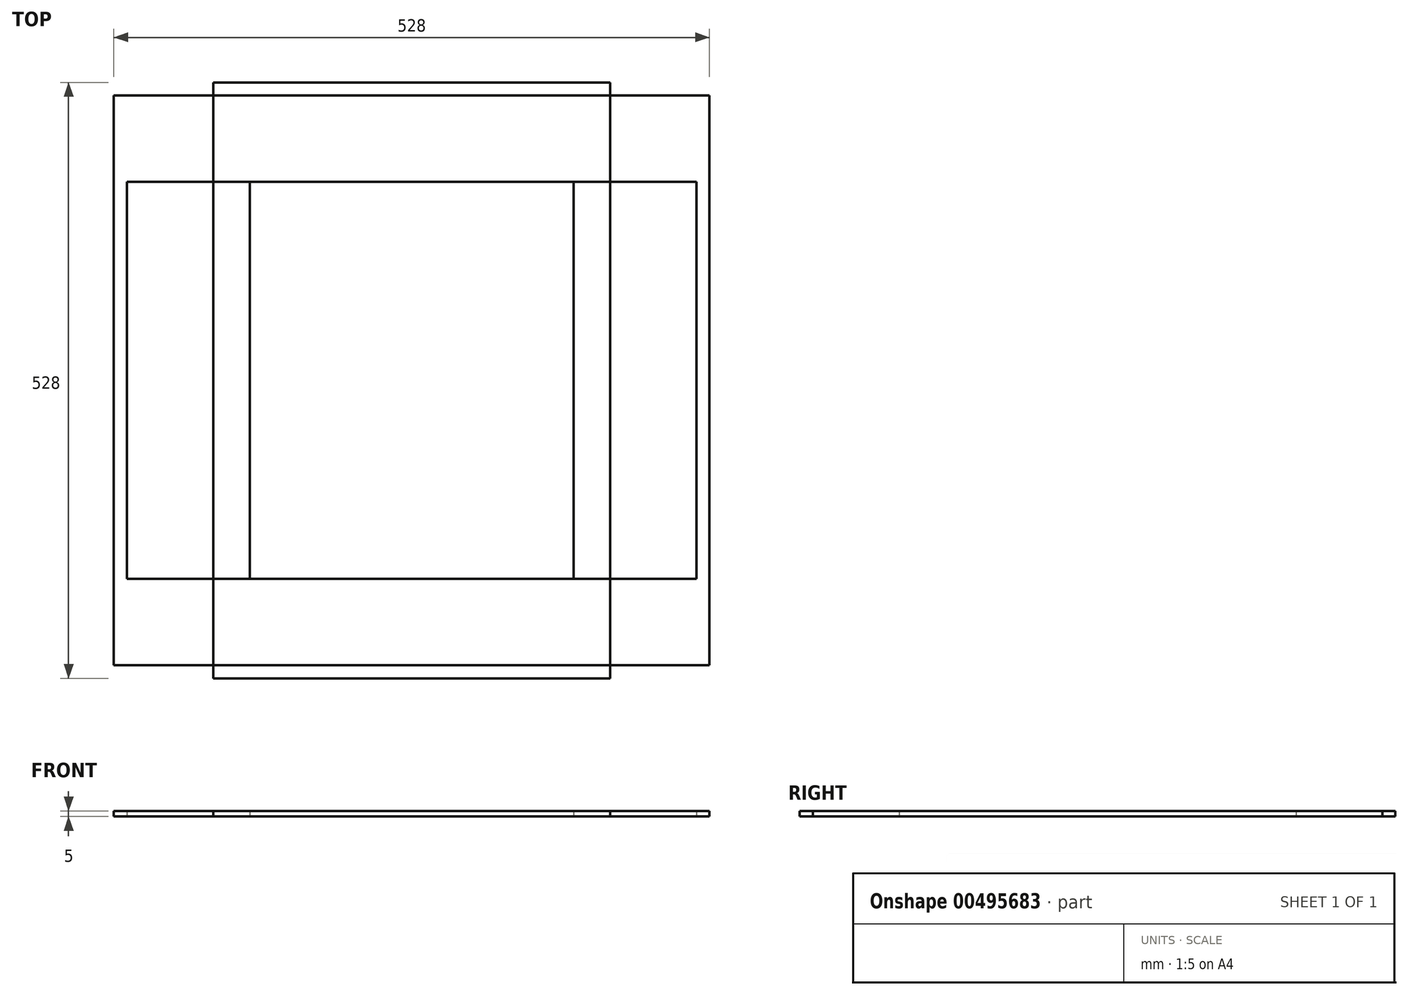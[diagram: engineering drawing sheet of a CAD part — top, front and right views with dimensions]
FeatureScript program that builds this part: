
annotation { "Feature Type Name" : "Feature", "Feature Type Description" : "" }
export const myFeature = defineFeature(function(context is Context, id is Id, definition is map)
    precondition{}
    {
        {
            var Q0;
            Q0=qCreatedBy(makeId("Top.planeOp"),FACE);
            var sketch = newSketch(context, id + "F0", { "sketchPlane" : qUnion([Q0])});
            skLineSegment(sketch, "E0.bottom", {"start": v(252.5, 176) * mm, "end": v(-252.5, 176) * mm});
            skLineSegment(sketch, "E0.top", {"start": v(252.5, -176) * mm, "end": v(-252.5, -176) * mm});
            skLineSegment(sketch, "E0.left", {"start": v(252.5, 176) * mm, "end": v(252.5, -176) * mm});
            skLineSegment(sketch, "E0.right", {"start": v(-252.5, 176) * mm, "end": v(-252.5, -176) * mm});
            skPoint(sketch, "E0.middle", {"position": v(0, 0) * mm});
            skSolve(sketch);
        }
        {
            var Q0;
            Q0 = qSketchRegion(id + "F0", true);
            extrude(context, id + "F1", {"entities" : qUnion([Q0]), "depth" : 5 * mm});
        }
        {
            var Q0;
            Q0=qCreatedBy(makeId("Top.planeOp"),FACE);
            var sketch = newSketch(context, id + "F2", { "sketchPlane" : qUnion([Q0])});
            skLineSegment(sketch, "E1.bottom", {"start": v(264, 252.5) * mm, "end": v(-264, 252.5) * mm});
            skLineSegment(sketch, "E1.top", {"start": v(264, -252.5) * mm, "end": v(-264, -252.5) * mm});
            skLineSegment(sketch, "E1.left", {"start": v(264, 252.5) * mm, "end": v(264, -252.5) * mm});
            skLineSegment(sketch, "E1.right", {"start": v(-264, 252.5) * mm, "end": v(-264, -252.5) * mm});
            skPoint(sketch, "E1.middle", {"position": v(0, 0) * mm});
            skSolve(sketch);
        }
        {
            var Q0;
            Q0=makeQuery(id+"F2.imprint","IMPRINT",FACE,{"disambiguationData":[TD([[makeQuery(id+"F2.imprint","IMPRINT",EDGE,{"derivedFrom":sQuery(id+"F2.wireOp",EDGE,"E1.bottom")}),1.0]])]});
            extrude(context, id + "F3", {"entities" : qUnion([Q0]), "depth" : 5 * mm});
        }
        {
            var Q0;
            Q0=qCreatedBy(makeId("Top.planeOp"),FACE);
            var sketch = newSketch(context, id + "F4", { "sketchPlane" : qUnion([Q0])});
            skLineSegment(sketch, "E2.bottom", {"start": v(176, 264) * mm, "end": v(-176, 264) * mm});
            skLineSegment(sketch, "E2.top", {"start": v(176, -264) * mm, "end": v(-176, -264) * mm});
            skLineSegment(sketch, "E2.left", {"start": v(176, 264) * mm, "end": v(176, -264) * mm});
            skLineSegment(sketch, "E2.right", {"start": v(-176, 264) * mm, "end": v(-176, -264) * mm});
            skPoint(sketch, "E2.middle", {"position": v(0, 0) * mm});
            skSolve(sketch);
        }
        {
            var Q0;
            Q0 = qSketchRegion(id + "F4", true);
            extrude(context, id + "F5", {"entities" : qUnion([Q0]), "depth" : 5 * mm});
        }
        {
            var Q0;
            Q0=qCreatedBy(makeId("Top.planeOp"),FACE);
            var sketch = newSketch(context, id + "F6", { "sketchPlane" : qUnion([Q0])});
            skLineSegment(sketch, "E3.bottom", {"start": v(143.5, 176) * mm, "end": v(-143.5, 176) * mm});
            skLineSegment(sketch, "E3.top", {"start": v(143.5, -176) * mm, "end": v(-143.5, -176) * mm});
            skLineSegment(sketch, "E3.left", {"start": v(143.5, 176) * mm, "end": v(143.5, -176) * mm});
            skLineSegment(sketch, "E3.right", {"start": v(-143.5, 176) * mm, "end": v(-143.5, -176) * mm});
            skPoint(sketch, "E3.middle", {"position": v(0, 0) * mm});
            skSolve(sketch);
        }
        {
            var Q0;
            Q0=makeQuery(id+"F6.imprint","IMPRINT",FACE,{"disambiguationData":[TD([[makeQuery(id+"F6.imprint","IMPRINT",EDGE,{"derivedFrom":sQuery(id+"F6.wireOp",EDGE,"E3.bottom")}),1.0]])]});
            extrude(context, id + "F7", {"entities" : qUnion([Q0]), "depth" : 5 * mm});
        }
    });
